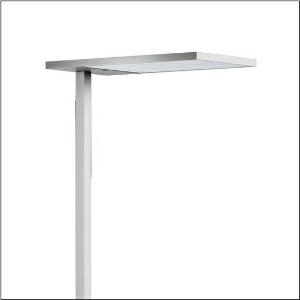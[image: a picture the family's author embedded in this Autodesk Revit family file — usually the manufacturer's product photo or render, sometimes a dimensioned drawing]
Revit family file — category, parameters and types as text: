
# Revit family: silica_r__21_floor_r_51mx53sg4ds_70f9
name_source: partatom
category: Lighting Fixtures
units: mm (PartAtom-declared; Revit-internal decimal feet)

## family parameters
Cut with Voids When Loaded = No
Host = Face
Light Source = No
Part Type = Normal
Room Calculation Point = No
Round Connector Dimension = Use Diameter
Shared = No

## types (1)
- Silica® 21 Floor R (1 x LED, 15000 lm, 106.4 W, 4000K)
    Apparent Load = 106 VA
    CIE Flux Codes = 54 86 97 13 100
    Color Rendering = 80
    Color Temperature = 4000K
    Default Elevation = 1800 mm
    Description = Silica® 21 Floor R, floorstanding luminaire, of PMMA, primary optical cover: prismatic diffuser, of PMMA, CAT 2 (L<= 3000cd/m²), light emission: indirect/direct distribution, primary light characteristic: symmetric, primary optical cover: cover panel, of PMMA, installation type: not mounted, LED, rated luminous flux: 15.000lm, luminous efficacy: 141lm/W, light colour: 840, colour temperature: 4000K, control gear: DALI 2, daylight-dependent control, mains connection: 230V, AC, 50/60Hz, connection cable included, cable length: 2,5m, rated input power: 106.4W, luminaire head, of aluminium, powder-coated, metallic grey (RAL 9006), length: 671mm, width: 371mm, height: 2010mm, supporting column, angular, of aluminium, powder-coated, metallic grey (RAL 9006), baseplate, of steel, powder-coated, metallic grey (RAL 9006), sensor module PR3-S, local control - self-sufficient standalone sensors, equipment: master, dimmable, protection rating (complete): IP20, insulation class (complete): insulation class I (protective earthing), certification: CE, standard: EN 50419, packaging unit: 1 piece
    Height = 18 mm
    Lamp = 1 x LED
    Lamp Light Flux = 15000 lm
    Lamp Power = 106.4 W
    Lamp count = 1
    Length = 650 mm
    Luminous efficacy = 141 lm/W
    Manufacturer = Siteco
    ModVariant = No
    Model = 51MX53SG4DS
    Mounting Place = Floor
    Mounting Type = Freestanding
    Number of Poles = 1
    OnlyDefault = Yes
    Power Factor = 1
    Product Name = Silica® 21 Floor R
    Product group = floorstanding luminaire
    ProductGroupID = 1302
    Protection Class = Protection class I
    Protection Degree = IP 20
    RLX_Detail_Level = 1
    RLX_Emergency_Light_Flux = 0 lm
    RLX_Emergency_Type = 0
    RLX_Emergency_Type_DB = No
    RlxData = <blob elided: 20425 chars, md5=ddaa3e8e>
    Socket = socket
    Standby Power = 0 W
    System Light Flux = 15000 lm
    System Power = 106 W
    Type Comments = Product without accessories
    Type Image = l_1006716.jpg
    URL = http://relux.com
    VarID = ---
    Voltage = 0 V
    Weight = 0.00 kg
    Width = 350 mm

## geometry (parser evidence)
native form markers: Blend x4, Sweep x15
no freeform markers — native parametric forms only
